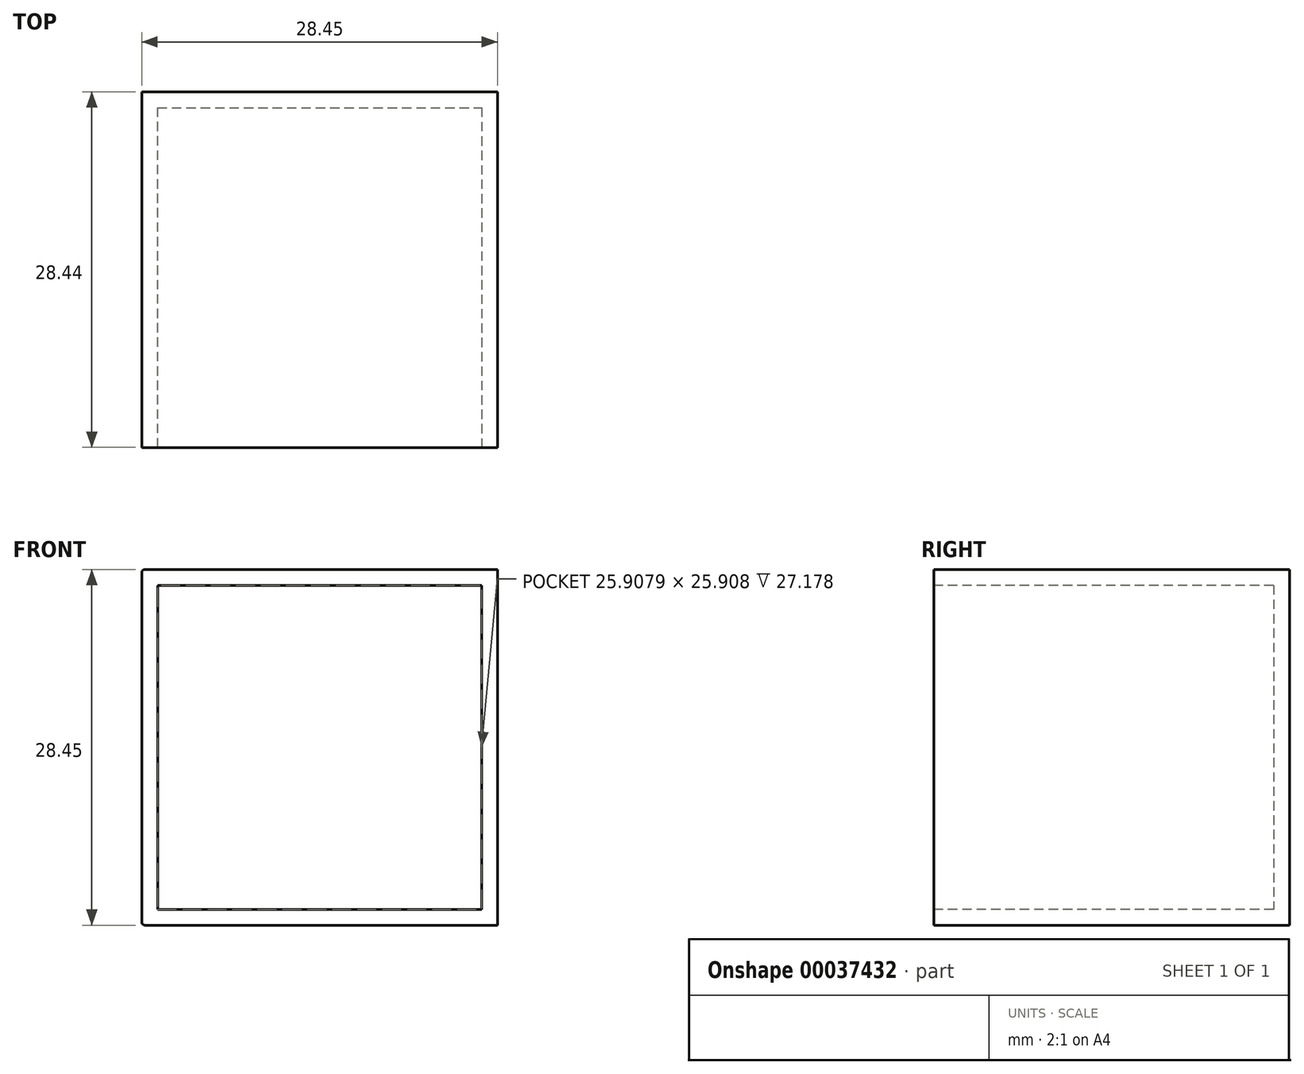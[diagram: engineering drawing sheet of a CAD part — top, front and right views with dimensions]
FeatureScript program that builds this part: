
annotation { "Feature Type Name" : "Feature", "Feature Type Description" : "" }
export const myFeature = defineFeature(function(context is Context, id is Id, definition is map)
    precondition{}
    {
        {
            var Q0;
            Q0=qCreatedBy(makeId("Top.planeOp"),FACE);
            var sketch = newSketch(context, id + "F0", { "sketchPlane" : qUnion([Q0])});
            skLineSegment(sketch, "E0.rect.bottom", {"start": v(-30.56, 36.4) * mm, "end": v(30.56, 36.4) * mm});
            skLineSegment(sketch, "E0.rect.top", {"start": v(-30.56, -36.4) * mm, "end": v(30.56, -36.4) * mm});
            skLineSegment(sketch, "E0.rect.left", {"start": v(-30.56, 36.4) * mm, "end": v(-30.56, -36.4) * mm});
            skLineSegment(sketch, "E0.rect.right", {"start": v(30.56, 36.4) * mm, "end": v(30.56, -36.4) * mm});
            skPoint(sketch, "E0.rect.middle", {"position": v(0, 0) * mm});
            skSolve(sketch);
        }
        {
            var Q0;
            Q0 = qSketchRegion(id + "F0", true);
            extrude(context, id + "F1", {"entities" : qUnion([Q0]), "depth" : 28.45 * mm});
        }
        {
            var Q0;
            Q0=makeQuery(id+"F1.opExtrude","SWEPT_FACE",FACE,{"disambiguationData":[OSD([sQuery(id+"F0.wireOp",EDGE,"E0.rect.right")])]});
            extrude(context, id + "F2", {"entities" : qUnion([Q0]), "operationType" : NewBodyOperationType.REMOVE, "oppositeDirection" : true, "depth" : 32.68 * mm});
        }
        {
            var Q0;
            Q0=makeQuery(id+"F1.opExtrude","SWEPT_FACE",FACE,{"disambiguationData":[OSD([sQuery(id+"F0.wireOp",EDGE,"E0.rect.top")])]});
            extrude(context, id + "F3", {"entities" : qUnion([Q0]), "operationType" : NewBodyOperationType.REMOVE, "oppositeDirection" : true, "depth" : 41.04 * mm});
        }
        {
            var Q0;
            {var subQ0=sQuery(id+"F0.wireOp",EDGE,"E0.rect.right");Q0=makeQuery(id+"F2.boolean.opBoolean","COPY",EDGE,{"derivedFrom":makeQuery(id+"F2.opExtrude","CAP_EDGE",EDGE,{"disambiguationData":[OSD([subQ0]),TDD([makeQuery(id+"F1.opExtrude","CAP_EDGE",EDGE,{"disambiguationData":[OSD([subQ0])],"isStart":false})])],"isStart":false})});}
            var Q1;
            Q1=makeQuery(id+"F1.opExtrude","CAP_EDGE",EDGE,{"disambiguationData":[OSD([sQuery(id+"F0.wireOp",EDGE,"E0.rect.left")])],"isStart":false});
            var Q2;
            {var subQ0=sQuery(id+"F0.wireOp",EDGE,"E0.rect.right");Q2=makeQuery(id+"F2.boolean.opBoolean","COPY",EDGE,{"derivedFrom":makeQuery(id+"F2.opExtrude","CAP_EDGE",EDGE,{"disambiguationData":[OSD([subQ0]),TDD([makeQuery(id+"F1.opExtrude","CAP_EDGE",EDGE,{"disambiguationData":[OSD([subQ0])],"isStart":true})])],"isStart":false})});}
            var Q3;
            Q3=makeQuery(id+"F1.opExtrude","CAP_EDGE",EDGE,{"disambiguationData":[OSD([sQuery(id+"F0.wireOp",EDGE,"E0.rect.left")])],"isStart":true});
            fillet(context, id + "F4", {"entities" : qUnion([Q0, Q1, Q2, Q3]), "radius" : 0.25 * mm, "tangentPropagation" : true, "allowEdgeOverflow" : false});
        }
        {
            var Q0;
            Q0=makeQuery(id+"F3.boolean.opBoolean","COPY",FACE,{"derivedFrom":makeQuery(id+"F3.opExtrude","CAP_FACE",FACE,{"disambiguationData":[OSD([sQuery(id+"F0.wireOp",EDGE,"E0.rect.top")])],"isStart":false})});
            shell(context, id + "F5", {"entities" : qUnion([Q0]), "thickness" : 1.27 * mm});
        }
        {
            var Q0;
            Q0=makeQuery(id+"F3.boolean.opBoolean","COPY",FACE,{"derivedFrom":makeQuery(id+"F3.opExtrude","CAP_FACE",FACE,{"disambiguationData":[OSD([sQuery(id+"F0.wireOp",EDGE,"E0.rect.top")])],"isStart":false})});
            extrude(context, id + "F6", {"entities" : qUnion([Q0]), "operationType" : NewBodyOperationType.REMOVE, "oppositeDirection" : true, "depth" : 3.3 * mm});
        }
    });
